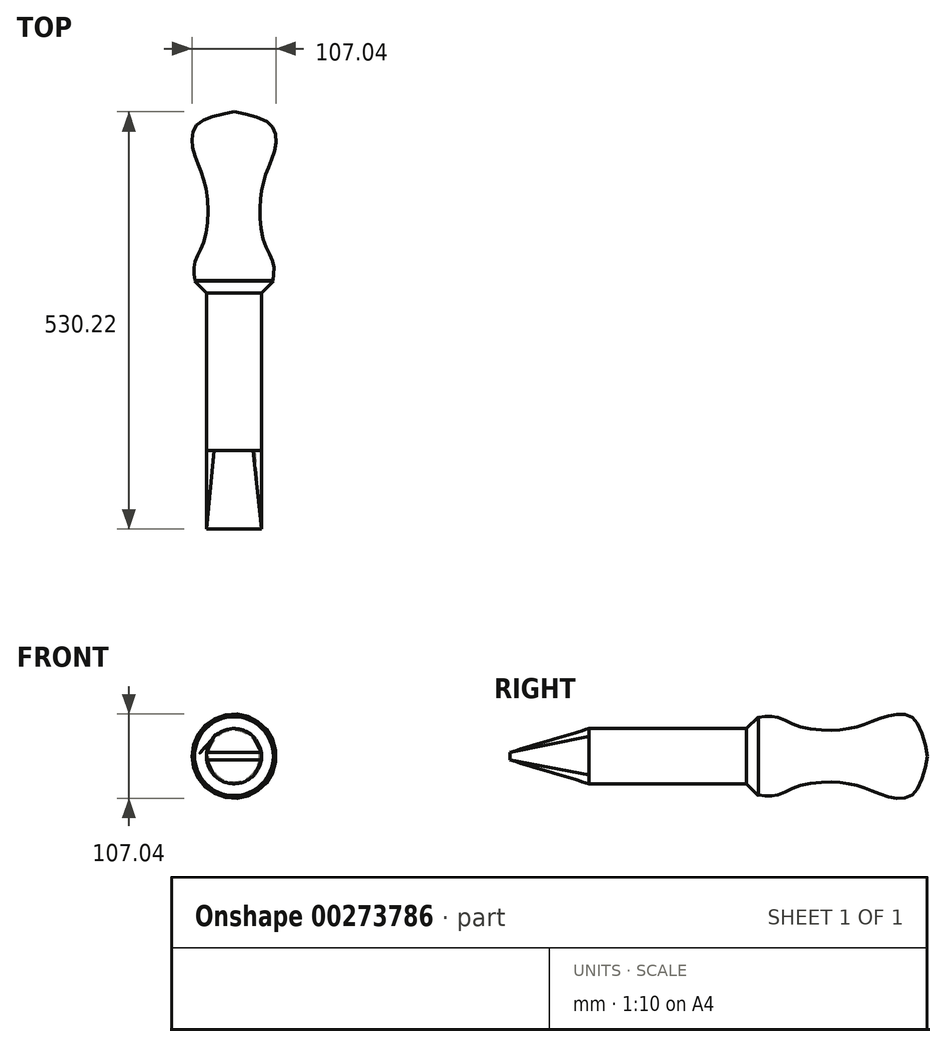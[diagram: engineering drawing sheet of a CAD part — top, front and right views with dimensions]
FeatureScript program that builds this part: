
annotation { "Feature Type Name" : "Feature", "Feature Type Description" : "" }
export const myFeature = defineFeature(function(context is Context, id is Id, definition is map)
    precondition{}
    {
        {
            var Q0;
            Q0=qCreatedBy(makeId("Front.planeOp"),FACE);
            var sketch = newSketch(context, id + "F0", { "sketchPlane" : qUnion([Q0])});
            skLineSegment(sketch, "E0.bottom", {"start": v(35, -5) * mm, "end": v(-35, -5) * mm});
            skLineSegment(sketch, "E0.top", {"start": v(35, 5) * mm, "end": v(-35, 5) * mm});
            skLineSegment(sketch, "E0.left", {"start": v(35, -5) * mm, "end": v(35, 5) * mm});
            skLineSegment(sketch, "E0.right", {"start": v(-35, -5) * mm, "end": v(-35, 5) * mm});
            skPoint(sketch, "E0.middle", {"position": v(0, 0) * mm});
            skSolve(sketch);
        }
        {
            var Q0;
            Q0=qCreatedBy(makeId("Front.planeOp"),FACE);
            cPlane(context, id + "F1", {"entities" : qUnion([Q0]), "cplaneType" : CPlaneType.OFFSET, "offset" : 100 * mm, "oppositeDirection" : true, "width" : 150 * mm, "height" : 150 * mm});
        }
        {
            var Q0;
            Q0=qCreatedBy(id+"F1.planeOp",FACE);
            var sketch = newSketch(context, id + "F2", { "sketchPlane" : qUnion([Q0])});
            skArc(sketch, "E1", {"start": v(24.22, 25.27) * mm, "mid": v(-0.68, 35) * mm, "end": v(-25.18, 24.31) * mm});
            skArc(sketch, "E2", {"start": v(-25.18, 24.31) * mm, "mid": v(-35, -0.36) * mm, "end": v(-24.67, -24.82) * mm});
            skArc(sketch, "E3", {"start": v(25.85, -23.6) * mm, "mid": v(34.98, 1.17) * mm, "end": v(24.22, 25.27) * mm});
            skArc(sketch, "E4", {"start": v(-24.67, -24.82) * mm, "mid": v(0.85, -34.99) * mm, "end": v(25.85, -23.6) * mm});
            skSolve(sketch);
        }
        {
            var Q0;
            Q0=makeQuery(id+"F2.imprint","IMPRINT",FACE,{"disambiguationData":[TD([[makeQuery(id+"F2.imprint","IMPRINT",EDGE,{"derivedFrom":sQuery(id+"F2.wireOp",EDGE,"E1")}),1.0]])]});
            var Q1;
            Q1=makeQuery(id+"F0.imprint","IMPRINT",FACE,{"disambiguationData":[TD([[makeQuery(id+"F0.imprint","IMPRINT",EDGE,{"derivedFrom":sQuery(id+"F0.wireOp",EDGE,"E0.bottom")}),-1.0]])]});
            loft(context, id + "F3", {"sheetProfilesArray" : [{ "sheetProfileEntities" : qUnion([Q0]) }, { "sheetProfileEntities" : qUnion([Q1]) }]});
        }
        {
            var Q0;
            Q0=qCreatedBy(id+"F1.planeOp",FACE);
            cPlane(context, id + "F4", {"entities" : qUnion([Q0]), "cplaneType" : CPlaneType.OFFSET, "offset" : 200 * mm, "oppositeDirection" : true, "width" : 150 * mm, "height" : 150 * mm});
        }
        {
            var Q0;
            Q0=qCreatedBy(id+"F4.planeOp",FACE);
            var sketch = newSketch(context, id + "F5", { "sketchPlane" : qUnion([Q0])});
            skCircle(sketch, "E5", {"center": v(0, 0) * mm, "radius": 35 * mm});
            skSolve(sketch);
        }
        {
            var Q1;
            Q1=makeQuery(id+"F3.opLoft","CAP_FACE",FACE,{"disambiguationData":[OSD([makeQuery(id+"F2.imprint","IMPRINT",FACE,{"disambiguationData":[TD([[makeQuery(id+"F2.imprint","IMPRINT",EDGE,{"derivedFrom":sQuery(id+"F2.wireOp",EDGE,"E1")}),1.0]])]})])],"isStart":true});
            var Q2;
            Q2=makeQuery(id+"F5.imprint","IMPRINT",FACE,{"disambiguationData":[TD([[makeQuery(id+"F5.imprint","IMPRINT",EDGE,{"derivedFrom":sQuery(id+"F5.wireOp",EDGE,"E5")}),1.0]])]});
            loft(context, id + "F6", {"operationType" : NewBodyOperationType.ADD, "sheetProfilesArray" : [{ "sheetProfileEntities" : qUnion([Q1]) }, { "sheetProfileEntities" : qUnion([Q2]) }]});
        }
        {
            var Q0;
            Q0=qCreatedBy(id+"F4.planeOp",FACE);
            cPlane(context, id + "F7", {"entities" : qUnion([Q0]), "cplaneType" : CPlaneType.OFFSET, "offset" : 15 * mm, "oppositeDirection" : true, "width" : 150 * mm, "height" : 150 * mm});
        }
        {
            var Q0;
            Q0=qCreatedBy(id+"F7.planeOp",FACE);
            var sketch = newSketch(context, id + "F8", { "sketchPlane" : qUnion([Q0])});
            skCircle(sketch, "E6", {"center": v(0, 0) * mm, "radius": 50 * mm});
            skSolve(sketch);
        }
        {
            var Q1;
            Q1=makeQuery(id+"F8.imprint","IMPRINT",FACE,{"disambiguationData":[TD([[makeQuery(id+"F8.imprint","IMPRINT",EDGE,{"derivedFrom":sQuery(id+"F8.wireOp",EDGE,"E6")}),1.0]])]});
            var Q2;
            Q2=makeQuery(id+"F6.opLoft","CAP_FACE",FACE,{"disambiguationData":[OSD([makeQuery(id+"F5.imprint","IMPRINT",FACE,{"disambiguationData":[TD([[makeQuery(id+"F5.imprint","IMPRINT",EDGE,{"derivedFrom":sQuery(id+"F5.wireOp",EDGE,"E5")}),1.0]])]})])],"isStart":true});
            loft(context, id + "F9", {"operationType" : NewBodyOperationType.ADD, "sheetProfilesArray" : [{ "sheetProfileEntities" : qUnion([Q1]) }, { "sheetProfileEntities" : qUnion([Q2]) }]});
        }
        {
            var Q0;
            Q0=qCreatedBy(makeId("Top.planeOp"),FACE);
            var sketch = newSketch(context, id + "F10", { "sketchPlane" : qUnion([Q0])});
            skLineSegment(sketch, "E7", {"start": v(0, 315.52) * mm, "end": v(-49.52, 315.52) * mm});
            skFitSpline(sketch, "E8", {"points": [v(-49.52, 315.52) * mm, v(-49.52, 339.71) * mm, v(-37.78, 365.65) * mm, v(-35.56, 433.08) * mm, v(-49.52, 473.66) * mm, v(-49.52, 510.26) * mm, v(0, 530.22) * mm], "startDerivative": vector(-23.9, 197.7) * mm, "endDerivative": vector(328.37, 66.14) * mm});
            skLineSegment(sketch, "E9", {"start": v(0, 530.22) * mm, "end": v(0, 315.52) * mm});
            skSolve(sketch);
        }
        {
            var Q0;
            Q0=makeQuery(id+"F10.imprint","IMPRINT",FACE,{"disambiguationData":[TD([[makeQuery(id+"F10.imprint","IMPRINT",EDGE,{"derivedFrom":sQuery(id+"F10.wireOp",EDGE,"E7")}),-1.0]])]});
            var Q1;
            Q1=sQuery(id+"F10.wireOp",EDGE,"E9");
            revolve(context, id + "F11", {"entities" : qUnion([Q0]), "axis" : qUnion([Q1]), "revolveType" : RevolveType.FULL});
        }
    });
